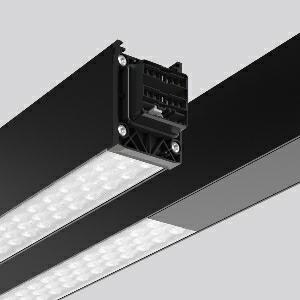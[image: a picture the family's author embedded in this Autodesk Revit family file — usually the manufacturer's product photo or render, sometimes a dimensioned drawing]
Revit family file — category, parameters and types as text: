
# Revit family: linedo_2_3m_30_1100_952330_853_776_504_f7b8
name_source: partatom
category: Lighting Fixtures
units: mm (PartAtom-declared; Revit-internal decimal feet)

## family parameters
Cut with Voids When Loaded = No
Host = Face
Light Source = No
Part Type = Normal
Room Calculation Point = No
Round Connector Dimension = Use Diameter
Shared = No

## types (1)
- LINEDO_2,3m_30_1100 (1 x LED Modul 850, 5200 lm, 5000)
    Apparent Load = 71 VA
    CIE Flux Codes = 89 97 99 100 100
    Color Rendering = 80
    Color Temperature = 5000
    Default Elevation = 1800 mm
    Description = LINEDO, 71 W, 10400 lm, 850, black, DALI
Continuous line luminaire, L 2291 B 58 H 76
    Height = 76 mm
    Lamp = 1 x LED Modul 850
    Lamp Light Flux = 5200 lm
    Lamp count = 1
    Length = 2291 mm
    Lifetime = 50000 h
    Luminous efficacy = 146 lm/W
    Manufacturer = RZB
    ModVariant = No
    Model = 952330.853.776.504
    Mounting Place = Ceiling
    Mounting Type = Surface mounted, Pendant
    Number of Poles = 1
    OnlyDefault = Yes
    Power Factor = 1
    Product Name = LINEDO_2,3m_30_1100
    Product group = Surface mounted continuous line luminaire system
    ProductGroupID = 310
    Protection Class = Protection class I
    Protection Degree = IP 54
    RLX_Detail_Level = 1
    RLX_Emergency_Light_Flux = 0 lm
    RLX_Emergency_Type = 0
    RLX_Emergency_Type_DB = No
    RlxData = <blob elided: 56589 chars, md5=e05f5fcf>
    Socket = socket
    Standby Power = 0 W
    System Light Flux = 10400 lm
    System Power = 71 W
    Type Comments = Product without accessories
    Type Image = 954530.853.476.504.jpg
    URL = http://relux.com
    VarID = ---
    Voltage = 230 V
    Voltage Range = 220-240 V
    Weight = 0.00 kg
    Width = 58 mm

## geometry (parser evidence)
native form markers: Blend x4, Sweep x15
no freeform markers — native parametric forms only
